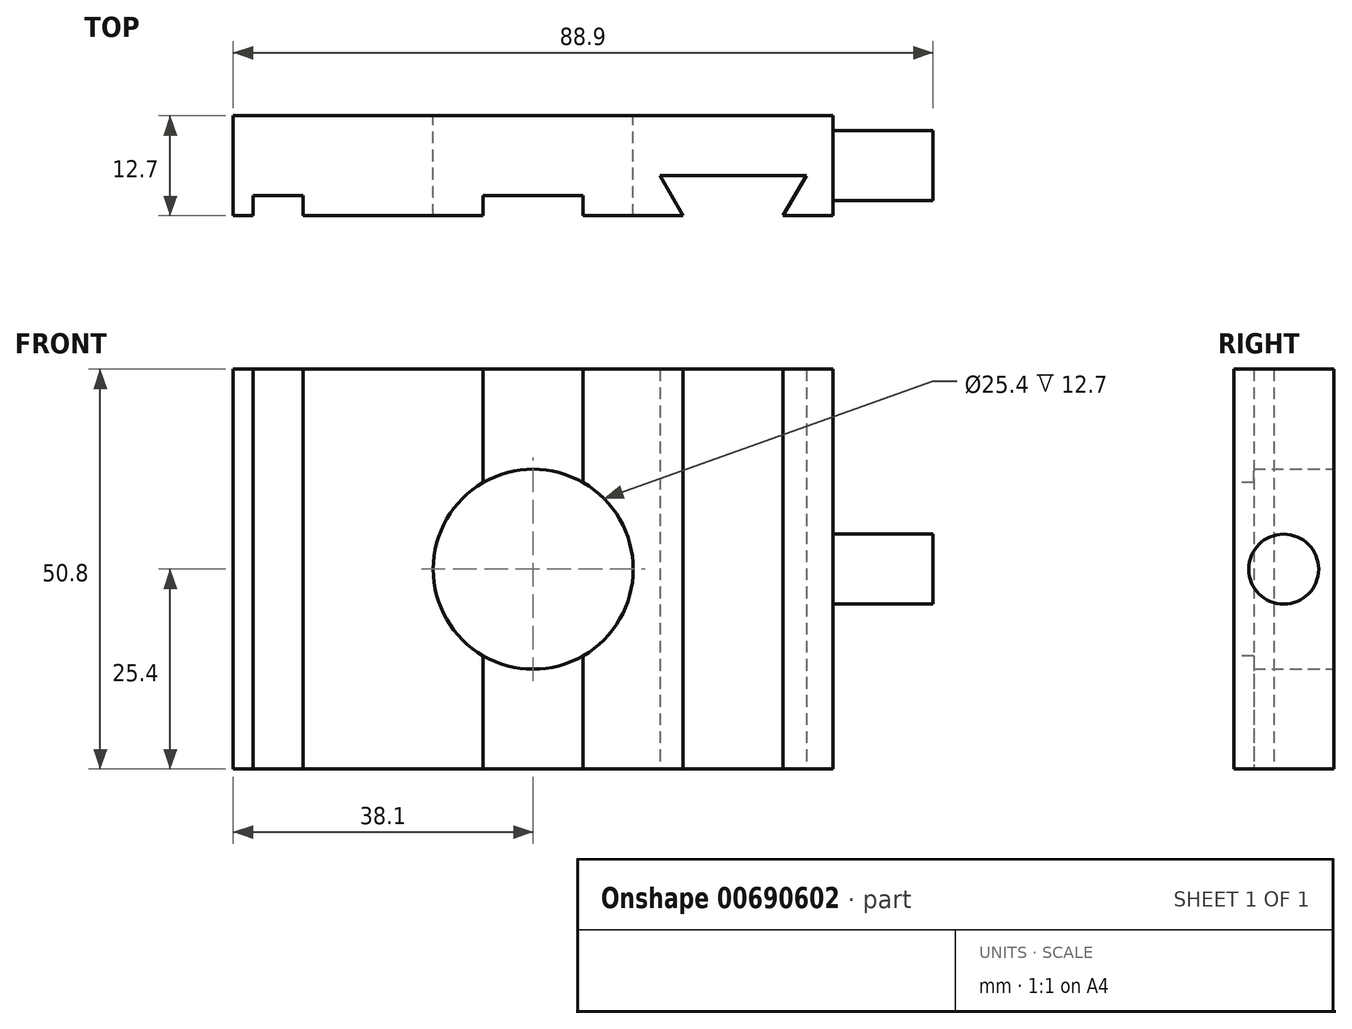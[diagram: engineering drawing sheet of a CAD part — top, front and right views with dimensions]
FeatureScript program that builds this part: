
annotation { "Feature Type Name" : "Feature", "Feature Type Description" : "" }
export const myFeature = defineFeature(function(context is Context, id is Id, definition is map)
    precondition{}
    {
        {
            var Q0;
            Q0=qCreatedBy(makeId("Front.planeOp"),FACE);
            var sketch = newSketch(context, id + "F0", { "sketchPlane" : qUnion([Q0])});
            skLineSegment(sketch, "E0.bottom", {"start": v(38.1, -25.4) * mm, "end": v(-38.1, -25.4) * mm});
            skLineSegment(sketch, "E0.top", {"start": v(38.1, 25.4) * mm, "end": v(-38.1, 25.4) * mm});
            skLineSegment(sketch, "E0.left", {"start": v(38.1, -25.4) * mm, "end": v(38.1, 25.4) * mm});
            skLineSegment(sketch, "E0.right", {"start": v(-38.1, -25.4) * mm, "end": v(-38.1, 25.4) * mm});
            skPoint(sketch, "E0.middle", {"position": v(0, 0) * mm});
            skCircle(sketch, "E1", {"center": v(0, 0) * mm, "radius": 12.7 * mm});
            skSolve(sketch);
        }
        {
            var Q0;
            Q0=makeQuery(id+"F0.imprint","IMPRINT",FACE,{"disambiguationData":[TD([[makeQuery(id+"F0.imprint","IMPRINT",EDGE,{"derivedFrom":sQuery(id+"F0.wireOp",EDGE,"E0.bottom")}),-1.0]])]});
            extrude(context, id + "F1", {"entities" : qUnion([Q0]), "depth" : 12.7 * mm, "offsetDistance" : 25.4 * mm});
        }
        {
            var Q0;
            Q0=makeQuery(id+"F1.opExtrude","CAP_FACE",FACE,{"disambiguationData":[OSD([sQuery(id+"F0.wireOp",EDGE,"E0.bottom"),sQuery(id+"F0.wireOp",EDGE,"E0.top"),sQuery(id+"F0.wireOp",EDGE,"E0.left"),sQuery(id+"F0.wireOp",EDGE,"E0.right"),sQuery(id+"F0.wireOp",EDGE,"E1")])],"isStart":false});
            var sketch = newSketch(context, id + "F2", { "sketchPlane" : qUnion([Q0])});
            skLineSegment(sketch, "E2.bottom", {"start": v(-35.56, 25.4) * mm, "end": v(-29.2, 25.4) * mm});
            skLineSegment(sketch, "E2.top", {"start": v(-35.56, -25.4) * mm, "end": v(-29.2, -25.4) * mm});
            skLineSegment(sketch, "E2.left", {"start": v(-35.56, 25.4) * mm, "end": v(-35.56, -25.4) * mm});
            skLineSegment(sketch, "E2.right", {"start": v(-29.2, 25.4) * mm, "end": v(-29.2, -25.4) * mm});
            skLineSegment(sketch, "E3", {"start": v(-6.35, 25.4) * mm, "end": v(-6.35, -25.4) * mm});
            skLineSegment(sketch, "E4", {"start": v(-6.35, -25.4) * mm, "end": v(6.35, -25.4) * mm});
            skLineSegment(sketch, "E5", {"start": v(6.35, -25.4) * mm, "end": v(6.35, 25.4) * mm});
            skLineSegment(sketch, "E6", {"start": v(6.35, 25.4) * mm, "end": v(-6.35, 25.4) * mm});
            skLineSegment(sketch, "E7", {"start": v(0, 25.4) * mm, "end": v(0, -25.4) * mm, "construction": true});
            skSolve(sketch);
        }
        {
            var Q0;
            Q0=makeQuery(id+"F2.imprint","IMPRINT",FACE,{"disambiguationData":[TD([[makeQuery(id+"F2.imprint","IMPRINT",EDGE,{"derivedFrom":sQuery(id+"F2.wireOp",EDGE,"E2.bottom")}),1.0]])]});
            var Q1;
            {var subQ0=sQuery(id+"F2.wireOp",EDGE,"E6");Q1=makeQuery(id+"F2.imprint","IMPRINT",FACE,{"disambiguationData":[TD([[makeQuery(id+"F2.imprint","IMPRINT",EDGE,{"derivedFrom":subQ0}),1.0]])]});}
            var Q2;
            {var subQ0=sQuery(id+"F2.wireOp",EDGE,"E4");Q2=makeQuery(id+"F2.imprint","IMPRINT",FACE,{"disambiguationData":[TD([[makeQuery(id+"F2.imprint","IMPRINT",EDGE,{"derivedFrom":subQ0}),-1.0]])]});}
            extrude(context, id + "F3", {"entities" : qUnion([Q0, Q1, Q2]), "operationType" : NewBodyOperationType.REMOVE, "oppositeDirection" : true, "depth" : 2.54 * mm, "offsetDistance" : 25.4 * mm});
        }
        {
            var Q0;
            Q0=makeQuery(id+"F1.opExtrude","SWEPT_FACE",FACE,{"disambiguationData":[OSD([sQuery(id+"F0.wireOp",EDGE,"E0.bottom")])]});
            var sketch = newSketch(context, id + "F4", { "sketchPlane" : qUnion([Q0])});
            skLineSegment(sketch, "E8", {"start": v(19.05, 12.7) * mm, "end": v(16.12, 7.62) * mm});
            skLineSegment(sketch, "E9", {"start": v(16.12, 7.62) * mm, "end": v(34.68, 7.62) * mm});
            skLineSegment(sketch, "E10", {"start": v(34.68, 7.62) * mm, "end": v(31.75, 12.7) * mm});
            skLineSegment(sketch, "E11", {"start": v(31.75, 12.7) * mm, "end": v(19.05, 12.7) * mm});
            skLineSegment(sketch, "E12", {"start": v(25.4, 12.7) * mm, "end": v(25.4, 7.62) * mm, "construction": true});
            skSolve(sketch);
        }
        {
            var Q0;
            Q0=makeQuery(id+"F4.imprint","IMPRINT",FACE,{"disambiguationData":[TD([[makeQuery(id+"F4.imprint","IMPRINT",EDGE,{"derivedFrom":sQuery(id+"F4.wireOp",EDGE,"E8")}),1.0]])]});
            extrude(context, id + "F5", {"entities" : qUnion([Q0]), "operationType" : NewBodyOperationType.REMOVE, "endBound" : BoundingType.THROUGH_ALL, "oppositeDirection" : true, "depth" : 25.4 * mm, "offsetDistance" : 25.4 * mm});
        }
        {
            var Q0;
            Q0=makeQuery(id+"F1.opExtrude","SWEPT_FACE",FACE,{"disambiguationData":[OSD([sQuery(id+"F0.wireOp",EDGE,"E0.left")])]});
            var sketch = newSketch(context, id + "F6", { "sketchPlane" : qUnion([Q0])});
            skCircle(sketch, "E13", {"center": v(-6.35, 0) * mm, "radius": 4.45 * mm});
            skPoint(sketch, "E13.centerSnap0", {"position": v(-6.35, -25.4) * mm});
            skPoint(sketch, "E13.centerSnap1", {"position": v(-12.7, 0) * mm});
            skSolve(sketch);
        }
        {
            var Q0;
            Q0=makeQuery(id+"F6.imprint","IMPRINT",FACE,{"disambiguationData":[TD([[makeQuery(id+"F6.imprint","IMPRINT",EDGE,{"derivedFrom":sQuery(id+"F6.wireOp",EDGE,"E13")}),1.0]])]});
            extrude(context, id + "F7", {"entities" : qUnion([Q0]), "operationType" : NewBodyOperationType.ADD, "depth" : 12.7 * mm, "offsetDistance" : 25.4 * mm});
        }
    });
